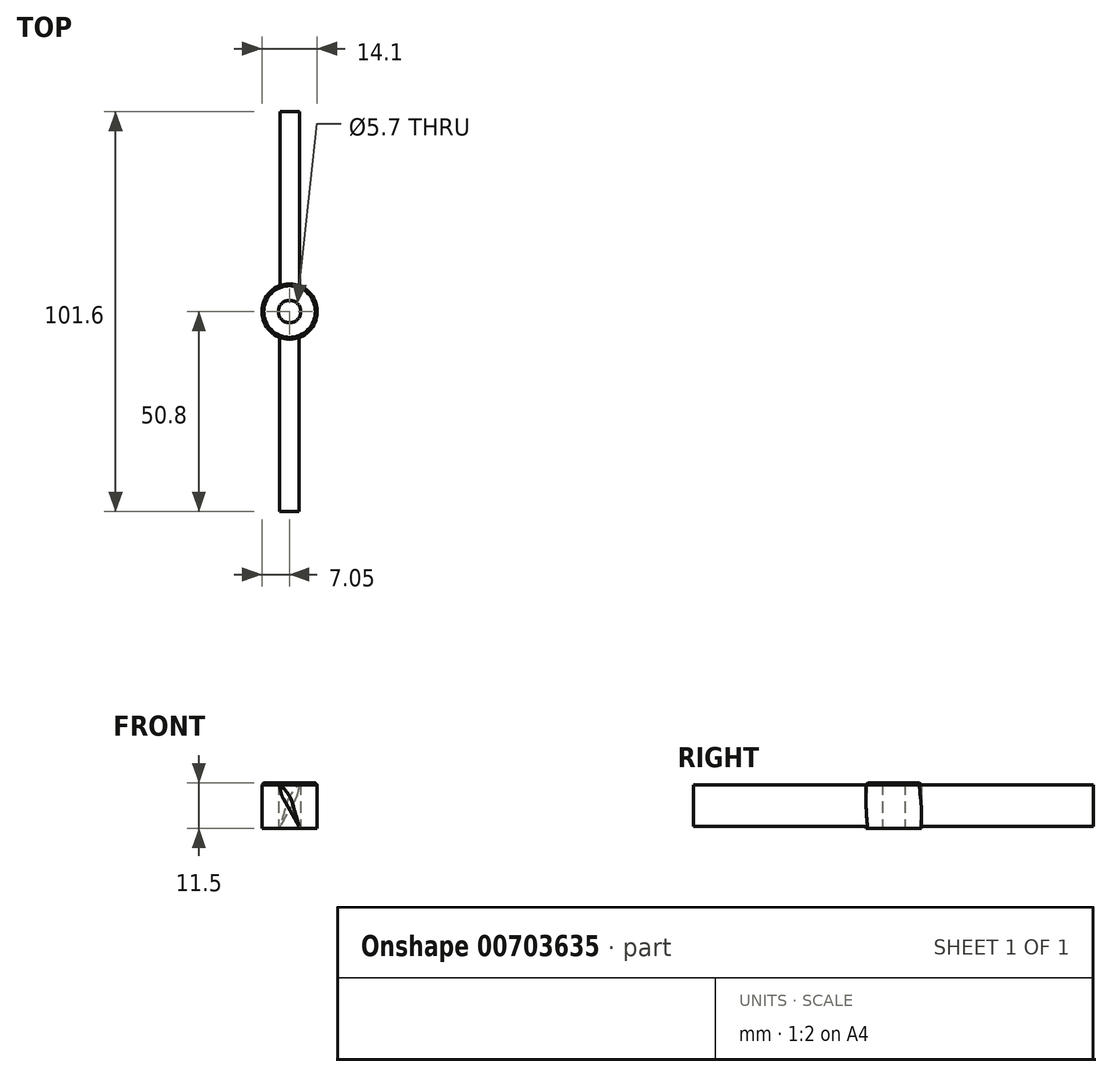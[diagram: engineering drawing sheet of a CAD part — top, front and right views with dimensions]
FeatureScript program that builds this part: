
annotation { "Feature Type Name" : "Feature", "Feature Type Description" : "" }
export const myFeature = defineFeature(function(context is Context, id is Id, definition is map)
    precondition{}
    {
        {
            var Q0;
            Q0=qCreatedBy(makeId("Top.planeOp"),FACE);
            var sketch = newSketch(context, id + "F0", { "sketchPlane" : qUnion([Q0])});
            skLineSegment(sketch, "E0", {"start": v(0, 0) * mm, "end": v(0, 50.8) * mm, "construction": true});
            skLineSegment(sketch, "E1", {"start": v(0, 0) * mm, "end": v(0, -50.8) * mm, "construction": true});
            skCircle(sketch, "E2", {"center": v(0, 0) * mm, "radius": 2.85 * mm});
            skCircle(sketch, "E3.0", {"center": v(0, 0) * mm, "radius": 7.05 * mm});
            skSolve(sketch);
        }
        {
            var Q0;
            Q0=makeQuery(id+"F0.imprint","IMPRINT",FACE,{"disambiguationData":[TD([[makeQuery(id+"F0.imprint","IMPRINT",EDGE,{"derivedFrom":sQuery(id+"F0.wireOp",EDGE,"E2")}),-1.0]])]});
            var Q1;
            Q1=makeQuery(id+"F0.imprint","IMPRINT",FACE,{"disambiguationData":[TD([[makeQuery(id+"F0.imprint","IMPRINT",EDGE,{"derivedFrom":sQuery(id+"F0.wireOp",EDGE,"E2")}),1.0]])]});
            extrude(context, id + "F1", {"entities" : qUnion([Q0, Q1]), "depth" : 11.5 * mm, "offsetDistance" : 25 * mm});
        }
        {
            var Q0;
            Q0=qCreatedBy(makeId("Front.planeOp"),FACE);
            var sketch = newSketch(context, id + "F2", { "sketchPlane" : qUnion([Q0])});
            skLineSegment(sketch, "E4", {"start": v(7.05, 6.9) * mm, "end": v(7.05, 0) * mm});
            skLineSegment(sketch, "E5", {"start": v(7.05, 0) * mm, "end": v(0, 0) * mm});
            skPoint(sketch, "E6", {"position": v(0, 5.75) * mm});
            skLineSegment(sketch, "E7", {"start": v(0, 0) * mm, "end": v(0, 11.5) * mm, "construction": true});
            skLineSegment(sketch, "E8.MirrorCS", {"start": v(-1.97, 8.16) * mm, "end": v(2.44, 0.52) * mm});
            skPoint(sketch, "E9.MirrorP", {"position": v(0.51, 3.84) * mm});
            skLineSegment(sketch, "E10.MirrorCS", {"start": v(0, 5.75) * mm, "end": v(-0.45, 5.54) * mm, "construction": true});
            skLineSegment(sketch, "E11.MirrorCS", {"start": v(0, 5.75) * mm, "end": v(0.82, 6.13) * mm, "construction": true});
            skLineSegment(sketch, "E12.MirrorCS", {"start": v(-2.44, 10.98) * mm, "end": v(2.44, 0.52) * mm, "construction": true});
            skFitSpline(sketch, "E13.MirrorCS", {"points": [v(-1.97, 8.16) * mm, v(-2.44, 10.98) * mm, v(-0.54, 8.99) * mm, v(0.67, 6.6) * mm, v(1.55, 3.56) * mm, v(2.44, 0.52) * mm], "startDerivative": vector(-4.14, 21.6) * mm, "endDerivative": vector(4.32, -14.36) * mm});
            skLineSegment(sketch, "E14.MirrorCS", {"start": v(0.9, 3.18) * mm, "end": v(1.55, 3.56) * mm, "construction": true});
            skLineSegment(sketch, "E15.MirrorCS", {"start": v(-0.63, 5.85) * mm, "end": v(0.67, 6.6) * mm, "construction": true});
            skLineSegment(sketch, "E16.MirrorCS", {"start": v(-3.3, 10.48) * mm, "end": v(-2.44, 10.98) * mm, "construction": true});
            skLineSegment(sketch, "E17.MirrorCS", {"start": v(-1.97, 8.16) * mm, "end": v(-0.54, 8.99) * mm, "construction": true});
            skLineSegment(sketch, "E18.MirrorCS", {"start": v(-0.63, 5.85) * mm, "end": v(2.44, 0.52) * mm, "construction": true});
            skLineSegment(sketch, "E19.MirrorCS", {"start": v(-0.63, 5.85) * mm, "end": v(-3.3, 10.48) * mm, "construction": true});
            skPoint(sketch, "E20.MirrorP", {"position": v(-0.3, 8.34) * mm});
            skSolve(sketch);
        }
        {
            var Q0;
            Q0=makeQuery(id+"F2.imprint","IMPRINT",FACE,{"disambiguationData":[TD([[makeQuery(id+"F2.imprint","IMPRINT",EDGE,{"derivedFrom":sQuery(id+"F2.wireOp",EDGE,"E8.MirrorCS")}),1.0]])]});
            extrude(context, id + "F3", {"entities" : qUnion([Q0]), "operationType" : NewBodyOperationType.ADD, "depth" : 50.8 * mm, "offsetDistance" : 25 * mm});
        }
        {
            var Q0;
            {var subQ0=sQuery(id+"F2.wireOp",EDGE,"msobF1Sl-cq8Q-FyCY-6Z0W-24ijWpGXxMAd");var subQ1=sQuery(id+"F2.wireOp",EDGE,"6ce1abe7-e2ef-4290-bca9-f703ce693d8b");Q0=makeQuery(id+"F3.opExtrude","SWEPT_EDGE",EDGE,{"disambiguationData":[OSD([subQ1,subQ0]),TDD([makeQuery(id+"F2.imprint","INTERSECT",VERTEX,{"disambiguationData":[OD(0.0)],"derivedFrom":[subQ1,subQ0]})])]});}
            var Q1;
            {var subQ0=sQuery(id+"F2.wireOp",EDGE,"E8.MirrorCS");var subQ1=sQuery(id+"F2.wireOp",EDGE,"E13.MirrorCS");Q1=makeQuery(id+"F3.boolean.opBoolean","SPLIT",EDGE,{"disambiguationData":[TD([makeQuery(id+"F1.opExtrude","SWEPT_FACE",FACE,{"disambiguationData":[OSD([sQuery(id+"F0.wireOp",EDGE,"E3.0")])]})])],"derivedFrom":makeQuery(id+"F3.opExtrude","SWEPT_EDGE",EDGE,{"disambiguationData":[OSD([subQ0,subQ1]),TDD([makeQuery(id+"F2.imprint","INTERSECT",VERTEX,{"disambiguationData":[OD(0.0)],"derivedFrom":[subQ0,subQ1]})])]})});}
            fillet(context, id + "F4", {"entities" : qUnion([Q0, Q1]), "radius" : 5 * mm, "tangentPropagation" : true, "allowEdgeOverflow" : false});
        }
        {
            var Q0;
            Q0=qCreatedBy(makeId("Front.planeOp"),FACE);
            var sketch = newSketch(context, id + "F5", { "sketchPlane" : qUnion([Q0])});
            skLineSegment(sketch, "E21", {"start": v(7.05, 6.9) * mm, "end": v(7.05, 0) * mm});
            skLineSegment(sketch, "E22", {"start": v(7.05, 0) * mm, "end": v(0, 0) * mm});
            skLineSegment(sketch, "E23", {"start": v(7.05, 4.07) * mm, "end": v(7.05, 0) * mm});
            skLineSegment(sketch, "E24", {"start": v(7.05, 3.95) * mm, "end": v(7.05, 5.45) * mm});
            skLineSegment(sketch, "E25", {"start": v(7.05, 4.95) * mm, "end": v(7.05, 3.75) * mm});
            skPoint(sketch, "E26.endSnap0", {"position": v(7.05, 2.04) * mm});
            skPoint(sketch, "E27", {"position": v(0, 5.75) * mm});
            skPoint(sketch, "E28", {"position": v(1.27, 4.24) * mm});
            skLineSegment(sketch, "E29", {"start": v(0, 0) * mm, "end": v(0, 11.5) * mm, "construction": true});
            skPoint(sketch, "E30.MirrorP", {"position": v(-0.51, 3.84) * mm});
            skLineSegment(sketch, "E31.MirrorCS", {"start": v(1.97, 8.16) * mm, "end": v(-2.44, 0.52) * mm});
            skLineSegment(sketch, "E32.MirrorCS", {"start": v(0, 5.75) * mm, "end": v(-0.82, 6.13) * mm, "construction": true});
            skLineSegment(sketch, "E33.MirrorCS", {"start": v(0, 5.75) * mm, "end": v(0.45, 5.54) * mm, "construction": true});
            skLineSegment(sketch, "E34.MirrorCS", {"start": v(0.63, 5.85) * mm, "end": v(-0.67, 6.6) * mm, "construction": true});
            skLineSegment(sketch, "E35.MirrorCS", {"start": v(3.3, 10.48) * mm, "end": v(2.44, 10.98) * mm, "construction": true});
            skLineSegment(sketch, "E36.MirrorCS", {"start": v(2.44, 10.98) * mm, "end": v(-2.44, 0.52) * mm, "construction": true});
            skLineSegment(sketch, "E37.MirrorCS", {"start": v(-0.9, 3.18) * mm, "end": v(-1.55, 3.56) * mm, "construction": true});
            skLineSegment(sketch, "E38.MirrorCS", {"start": v(0.63, 5.85) * mm, "end": v(3.3, 10.48) * mm, "construction": true});
            skLineSegment(sketch, "E39.MirrorCS", {"start": v(0.63, 5.85) * mm, "end": v(-2.44, 0.52) * mm, "construction": true});
            skLineSegment(sketch, "E40.MirrorCS", {"start": v(1.97, 8.16) * mm, "end": v(0.54, 8.99) * mm, "construction": true});
            skFitSpline(sketch, "E41.MirrorCS", {"points": [v(1.97, 8.16) * mm, v(2.44, 10.98) * mm, v(0.54, 8.99) * mm, v(-0.67, 6.6) * mm, v(-1.55, 3.56) * mm, v(-2.44, 0.52) * mm], "startDerivative": vector(4.14, 21.6) * mm, "endDerivative": vector(-4.32, -14.36) * mm});
            skSolve(sketch);
        }
        {
            var Q0;
            Q0=makeQuery(id+"F5.imprint","IMPRINT",FACE,{"disambiguationData":[TD([[makeQuery(id+"F5.imprint","IMPRINT",EDGE,{"derivedFrom":sQuery(id+"F5.wireOp",EDGE,"E31.MirrorCS")}),-1.0]])]});
            extrude(context, id + "F6", {"entities" : qUnion([Q0]), "operationType" : NewBodyOperationType.ADD, "oppositeDirection" : true, "depth" : 50.8 * mm, "offsetDistance" : 25 * mm});
        }
        {
            var Q0;
            {var subQ0=sQuery(id+"Fv6gQINzxOytYec_1.wireOp",EDGE,"d878019e-00ca-4c95-9281-a5dbebea3d630.MirrorCS");var subQ1=sQuery(id+"Fv6gQINzxOytYec_1.wireOp",EDGE,"19222e45-0a99-4dbb-b0f8-06b7d0d080b00.MirrorCS");Q0=makeQuery(id+"F6.opExtrude","SWEPT_EDGE",EDGE,{"disambiguationData":[OSD([subQ1,subQ0]),TDD([makeQuery(id+"Fv6gQINzxOytYec_1.imprint","INTERSECT",VERTEX,{"disambiguationData":[OD(0.0)],"derivedFrom":[subQ1,subQ0]})])]});}
            var Q1;
            {var subQ0=sQuery(id+"Fj0TBoSZPlOelra_1.wireOp",EDGE,"c5e6d0e3-df62-49b4-9d73-401119eaf40d2.MirrorCS");var subQ1=sQuery(id+"Fj0TBoSZPlOelra_1.wireOp",EDGE,"c5e6d0e3-df62-49b4-9d73-401119eaf40d1.MirrorCS");Q1=makeQuery(id+"F6.opExtrude","SWEPT_EDGE",EDGE,{"disambiguationData":[OSD([subQ1,subQ0]),TDD([makeQuery(id+"Fj0TBoSZPlOelra_1.imprint","INTERSECT",VERTEX,{"disambiguationData":[OD(0.0)],"derivedFrom":[subQ1,subQ0]})])]});}
            var Q2;
            {var subQ0=sQuery(id+"F5.wireOp",EDGE,"f684c9b4-9527-4a63-8f31-0619753b8ec57.MirrorCS");var subQ1=sQuery(id+"F5.wireOp",EDGE,"f684c9b4-9527-4a63-8f31-0619753b8ec52.MirrorCS");Q2=makeQuery(id+"F6.opExtrude","SWEPT_EDGE",EDGE,{"disambiguationData":[OSD([subQ1,subQ0]),TDD([makeQuery(id+"F5.imprint","INTERSECT",VERTEX,{"disambiguationData":[OD(0.0)],"derivedFrom":[subQ1,subQ0]})])]});}
            var Q3;
            {var subQ0=sQuery(id+"F5.wireOp",EDGE,"E31.MirrorCS");var subQ1=sQuery(id+"F5.wireOp",EDGE,"E41.MirrorCS");Q3=makeQuery(id+"F6.boolean.opBoolean","SPLIT",EDGE,{"disambiguationData":[TD([makeQuery(id+"F1.opExtrude","SWEPT_FACE",FACE,{"disambiguationData":[OSD([sQuery(id+"F0.wireOp",EDGE,"E3.0")])]})])],"derivedFrom":makeQuery(id+"F6.opExtrude","SWEPT_EDGE",EDGE,{"disambiguationData":[OSD([subQ0,subQ1]),TDD([makeQuery(id+"F5.imprint","INTERSECT",VERTEX,{"disambiguationData":[OD(0.0)],"derivedFrom":[subQ0,subQ1]})])]})});}
            fillet(context, id + "F7", {"entities" : qUnion([Q0, Q1, Q2, Q3]), "radius" : 5 * mm, "tangentPropagation" : true, "allowEdgeOverflow" : false});
        }
        {
            var Q0;
            Q0=makeQuery(id+"F1.opExtrude","CAP_EDGE",EDGE,{"disambiguationData":[OSD([sQuery(id+"F0.wireOp",EDGE,"E3.0")])],"isStart":false});
            chamfer(context, id + "F8", {"entities" : qUnion([Q0]), "width" : .5 * mm, "tangentPropagation" : true});
        }
        {
            var Q0;
            Q0=makeQuery(id+"F0.imprint","IMPRINT",FACE,{"disambiguationData":[TD([[makeQuery(id+"F0.imprint","IMPRINT",EDGE,{"derivedFrom":sQuery(id+"F0.wireOp",EDGE,"E2")}),1.0]])]});
            extrude(context, id + "F9", {"entities" : qUnion([Q0]), "operationType" : NewBodyOperationType.REMOVE, "depth" : 25 * mm, "offsetDistance" : 25 * mm});
        }
    });
